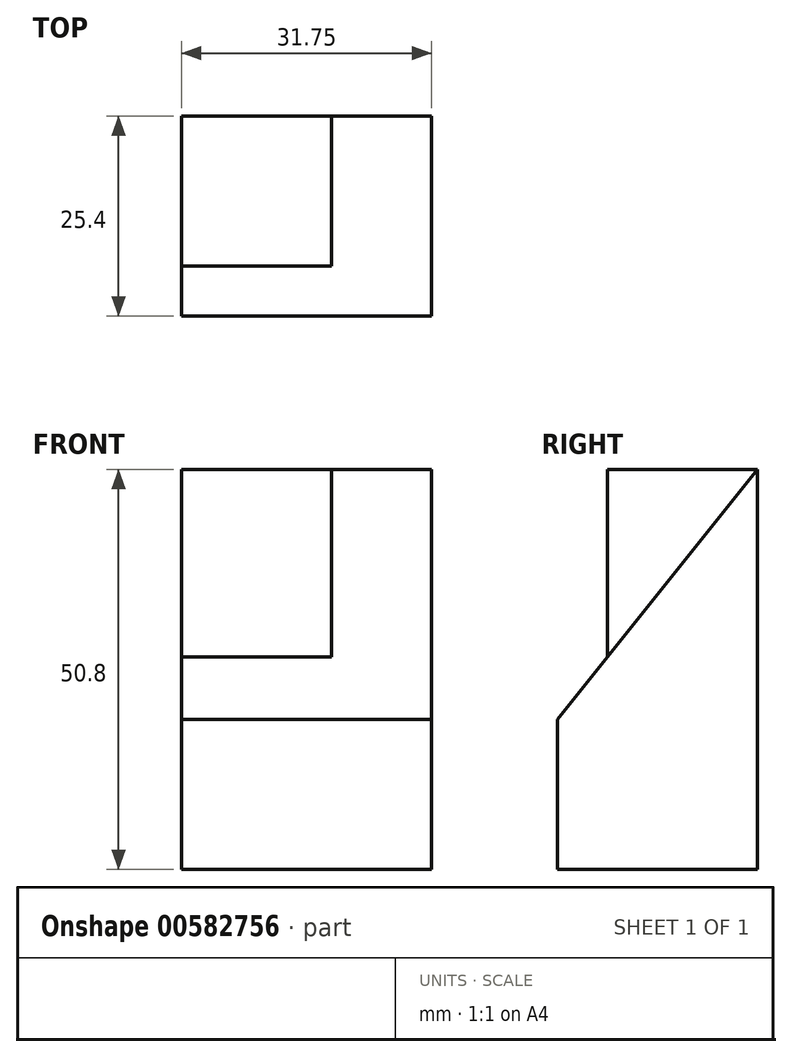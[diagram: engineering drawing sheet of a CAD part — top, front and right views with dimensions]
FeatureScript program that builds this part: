
annotation { "Feature Type Name" : "Feature", "Feature Type Description" : "" }
export const myFeature = defineFeature(function(context is Context, id is Id, definition is map)
    precondition{}
    {
        {
            var Q0;
            Q0=qCreatedBy(makeId("Front.planeOp"),FACE);
            var sketch = newSketch(context, id + "F0", { "sketchPlane" : qUnion([Q0])});
            skLineSegment(sketch, "E0", {"start": v(-53.83, 86.26) * mm, "end": v(-22.08, 86.26) * mm});
            skLineSegment(sketch, "E1", {"start": v(-22.08, 86.26) * mm, "end": v(-22.08, 35.46) * mm});
            skLineSegment(sketch, "E2", {"start": v(-22.08, 35.46) * mm, "end": v(-53.83, 35.46) * mm});
            skLineSegment(sketch, "E3", {"start": v(-53.83, 86.26) * mm, "end": v(-53.83, 35.46) * mm});
            skSolve(sketch);
        }
        {
            var Q0;
            Q0=makeQuery(id+"F0.imprint","IMPRINT",FACE,{"disambiguationData":[TD([[makeQuery(id+"F0.imprint","IMPRINT",EDGE,{"derivedFrom":sQuery(id+"F0.wireOp",EDGE,"E0")}),-1.0]])]});
            extrude(context, id + "F1", {"entities" : qUnion([Q0]), "depth" : 25.4 * mm, "offsetDistance" : 25.4 * mm});
        }
        {
            var Q0;
            Q0=makeQuery(id+"F1.opExtrude","SWEPT_FACE",FACE,{"disambiguationData":[OSD([sQuery(id+"F0.wireOp",EDGE,"E0")])]});
            var sketch = newSketch(context, id + "F2", { "sketchPlane" : qUnion([Q0])});
            skLineSegment(sketch, "E4", {"start": v(-53.83, 0) * mm, "end": v(-53.83, -19.05) * mm});
            skLineSegment(sketch, "E5", {"start": v(-53.83, -19.05) * mm, "end": v(-34.78, -19.05) * mm});
            skLineSegment(sketch, "E6", {"start": v(-34.78, -19.05) * mm, "end": v(-34.78, 0) * mm});
            skSolve(sketch);
        }
        {
            var Q0;
            Q0=makeQuery(id+"F1.opExtrude","SWEPT_FACE",FACE,{"disambiguationData":[OSD([sQuery(id+"F0.wireOp",EDGE,"E1")])]});
            var sketch = newSketch(context, id + "F3", { "sketchPlane" : qUnion([Q0])});
            skLineSegment(sketch, "E7", {"start": v(0, 86.26) * mm, "end": v(-25.4, 54.5) * mm});
            skSolve(sketch);
        }
        {
            var Q0;
            {var subQ0=sQuery(id+"F3.wireOp",EDGE,"E7");Q0=makeQuery(id+"F3.imprint","IMPRINT",FACE,{"disambiguationData":[TD([[makeQuery(id+"F3.imprint","IMPRINT",EDGE,{"derivedFrom":subQ0}),-1.0]])]});}
            extrude(context, id + "F4", {"entities" : qUnion([Q0]), "operationType" : NewBodyOperationType.REMOVE, "endBound" : BoundingType.THROUGH_ALL, "oppositeDirection" : true, "depth" : 25.4 * mm, "offsetDistance" : 25.4 * mm});
        }
        {
            var Q0;
            {var subQ0=sQuery(id+"F2.wireOp",EDGE,"E4");Q0=makeQuery(id+"F2.imprint","IMPRINT",FACE,{"disambiguationData":[TD([[makeQuery(id+"F2.imprint","IMPRINT",EDGE,{"derivedFrom":subQ0}),-1.0]])]});}
            extrude(context, id + "F5", {"entities" : qUnion([Q0]), "operationType" : NewBodyOperationType.ADD, "oppositeDirection" : true, "depth" : 50.55 * mm, "offsetDistance" : 25.4 * mm});
        }
    });
